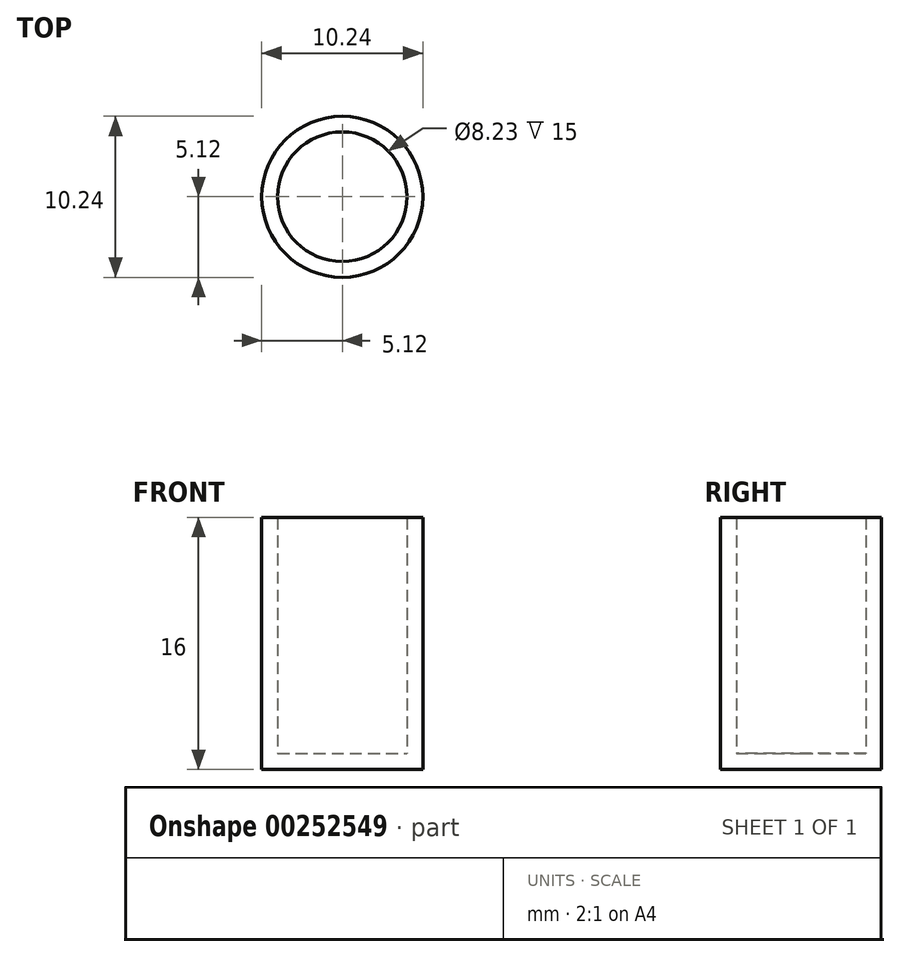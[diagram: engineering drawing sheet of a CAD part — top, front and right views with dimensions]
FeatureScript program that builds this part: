
annotation { "Feature Type Name" : "Feature", "Feature Type Description" : "" }
export const myFeature = defineFeature(function(context is Context, id is Id, definition is map)
    precondition{}
    {
        {
            var Q0;
            Q0=qCreatedBy(makeId("Front.planeOp"),FACE);
            var sketch = newSketch(context, id + "F0", { "sketchPlane" : qUnion([Q0])});
            skLineSegment(sketch, "E0.bottom", {"start": v(-4.54, -8) * mm, "end": v(5.12, -8) * mm});
            skLineSegment(sketch, "E0.top", {"start": v(-4.54, 8) * mm, "end": v(5.12, 8) * mm});
            skLineSegment(sketch, "E0.left", {"start": v(-4.54, -8) * mm, "end": v(-4.54, 8) * mm});
            skLineSegment(sketch, "E0.right", {"start": v(5.12, -8) * mm, "end": v(5.12, 8) * mm});
            skPoint(sketch, "E0.middle", {"position": v(0.29, 0) * mm});
            skLineSegment(sketch, "E1", {"start": v(0, 8) * mm, "end": v(0, -8) * mm});
            skLineSegment(sketch, "E2", {"start": v(0, -8) * mm, "end": v(0, 8) * mm});
            skSolve(sketch);
        }
        {
            var Q0;
            {var subQ0=sQuery(id+"F0.wireOp",EDGE,"E0.right");Q0=makeQuery(id+"F0.imprint","IMPRINT",FACE,{"disambiguationData":[TD([[makeQuery(id+"F0.imprint","IMPRINT",EDGE,{"derivedFrom":subQ0}),1.0]])]});}
            var Q1;
            Q1=sQuery(id+"F0.wireOp",EDGE,"E2");
            revolve(context, id + "F1", {"entities" : qUnion([Q0]), "axis" : qUnion([Q1]), "revolveType" : RevolveType.FULL});
        }
        {
            var Q0;
            Q0=makeQuery(id+"F1.opRevolve","SWEPT_FACE",FACE,{"disambiguationData":[OSD([sQuery(id+"F0.wireOp",EDGE,"E0.top")])]});
            shell(context, id + "F2", {"entities" : qUnion([Q0]), "thickness" : 1 * mm});
        }
    });
